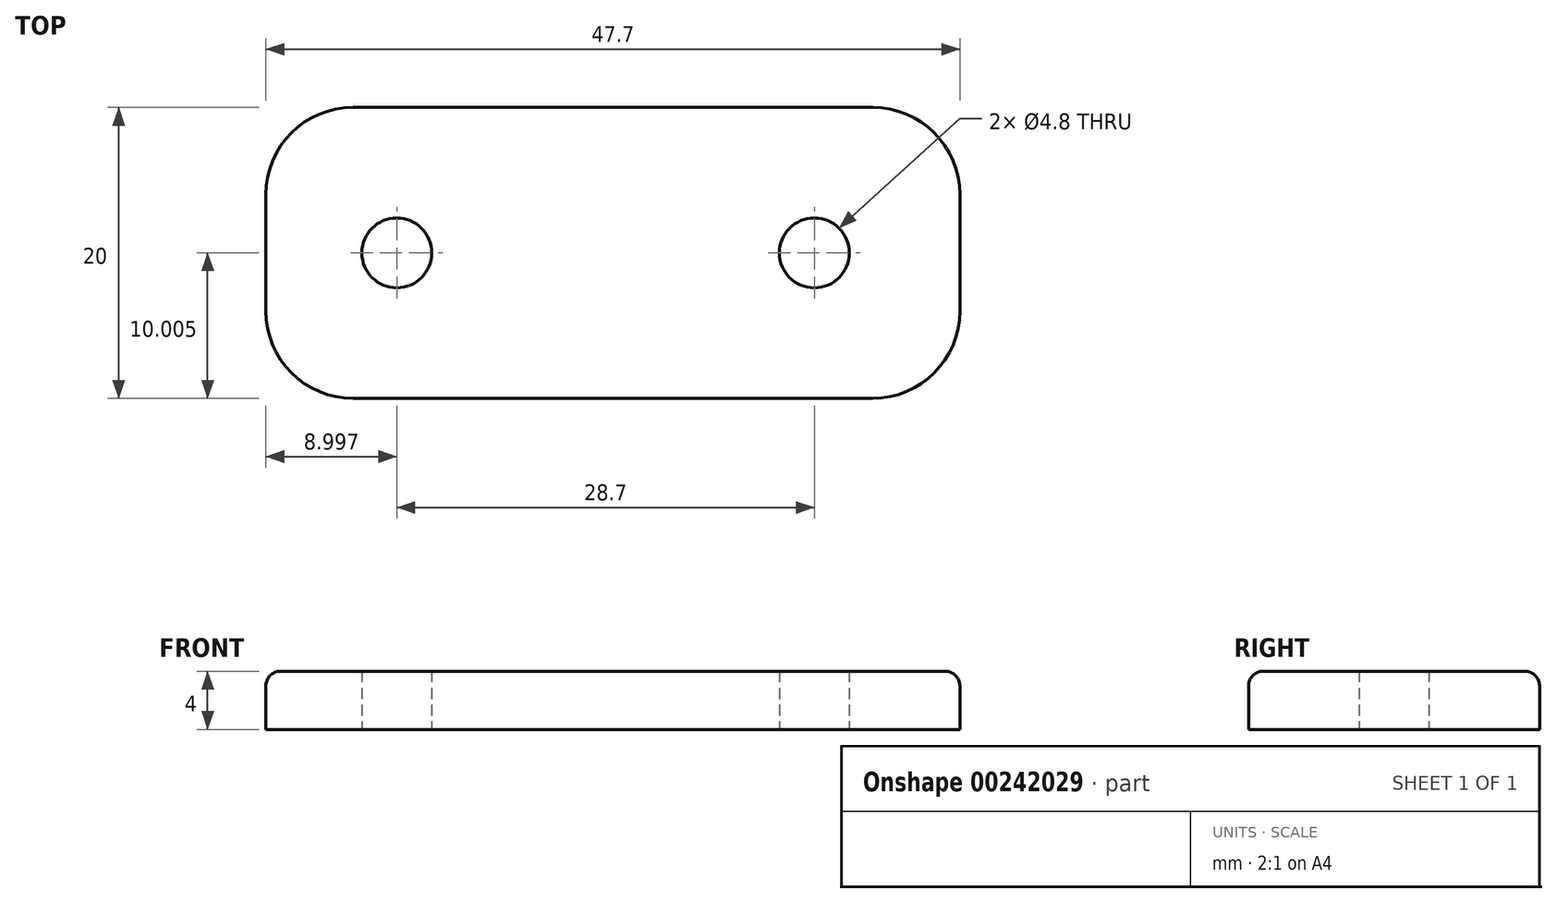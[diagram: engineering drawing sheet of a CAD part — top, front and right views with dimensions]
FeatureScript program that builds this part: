
annotation { "Feature Type Name" : "Feature", "Feature Type Description" : "" }
export const myFeature = defineFeature(function(context is Context, id is Id, definition is map)
    precondition{}
    {
        {
            var Q0;
            Q0=qCreatedBy(makeId("Top.planeOp"),FACE);
            var sketch = newSketch(context, id + "F0", { "sketchPlane" : qUnion([Q0])});
            skCircle(sketch, "E0", {"center": v(-55.34, 4.06) * mm, "radius": 2.4 * mm});
            skCircle(sketch, "E1", {"center": v(-26.64, 4.06) * mm, "radius": 2.4 * mm});
            skLineSegment(sketch, "E2.bottom", {"start": v(-64.34, 14.06) * mm, "end": v(-16.64, 14.06) * mm});
            skLineSegment(sketch, "E2.top", {"start": v(-64.34, -5.94) * mm, "end": v(-16.64, -5.94) * mm});
            skLineSegment(sketch, "E2.left", {"start": v(-64.34, 14.06) * mm, "end": v(-64.34, -5.94) * mm});
            skLineSegment(sketch, "E2.right", {"start": v(-16.64, 14.06) * mm, "end": v(-16.64, -5.94) * mm});
            skLineSegment(sketch, "E3", {"start": v(-29.04, 14.06) * mm, "end": v(-29.04, -5.94) * mm, "construction": true});
            skLineSegment(sketch, "E4", {"start": v(-52.94, 14.06) * mm, "end": v(-52.94, -5.94) * mm, "construction": true});
            skSolve(sketch);
        }
        {
            var Q0;
            Q0 = qSketchRegion(id + "F0", true);
            extrude(context, id + "F1", {"entities" : qUnion([Q0]), "flatOperationType" : FlatOperationType.REMOVE, "offsetDistance" : 25 * mm, "depth" : 4 * mm, "domain" : OperationDomain.MODEL});
        }
        {
            var Q0;
            Q0=makeQuery(id+"F1.opExtrude","SWEPT_EDGE",EDGE,{"disambiguationData":[OSD([sQuery(id+"F0.wireOp",EDGE,"E2.bottom"),sQuery(id+"F0.wireOp",EDGE,"E2.left")])]});
            var Q1;
            Q1=makeQuery(id+"F1.opExtrude","SWEPT_EDGE",EDGE,{"disambiguationData":[OSD([sQuery(id+"F0.wireOp",EDGE,"E2.bottom"),sQuery(id+"F0.wireOp",EDGE,"E2.right")])]});
            var Q2;
            Q2=makeQuery(id+"F1.opExtrude","SWEPT_EDGE",EDGE,{"disambiguationData":[OSD([sQuery(id+"F0.wireOp",EDGE,"E2.top"),sQuery(id+"F0.wireOp",EDGE,"E2.right")])]});
            var Q3;
            Q3=makeQuery(id+"F1.opExtrude","SWEPT_EDGE",EDGE,{"disambiguationData":[OSD([sQuery(id+"F0.wireOp",EDGE,"E2.top"),sQuery(id+"F0.wireOp",EDGE,"E2.left")])]});
            fillet(context, id + "F2", {"entities" : qUnion([Q0, Q1, Q2, Q3]), "radius" : 6 * mm, "tangentPropagation" : true, "defaultsChanged" : true, "vertexSettings" : [], "allowEdgeOverflow" : false});
        }
        {
            var Q0;
            Q0=makeQuery(id+"F1.opExtrude","CAP_EDGE",EDGE,{"disambiguationData":[OSD([sQuery(id+"F0.wireOp",EDGE,"E2.top")])],"isStart":false});
            fillet(context, id + "F3", {"entities" : qUnion([Q0]), "radius" : 1 * mm, "tangentPropagation" : true, "defaultsChanged" : true, "vertexSettings" : [], "allowEdgeOverflow" : false});
        }
    });
